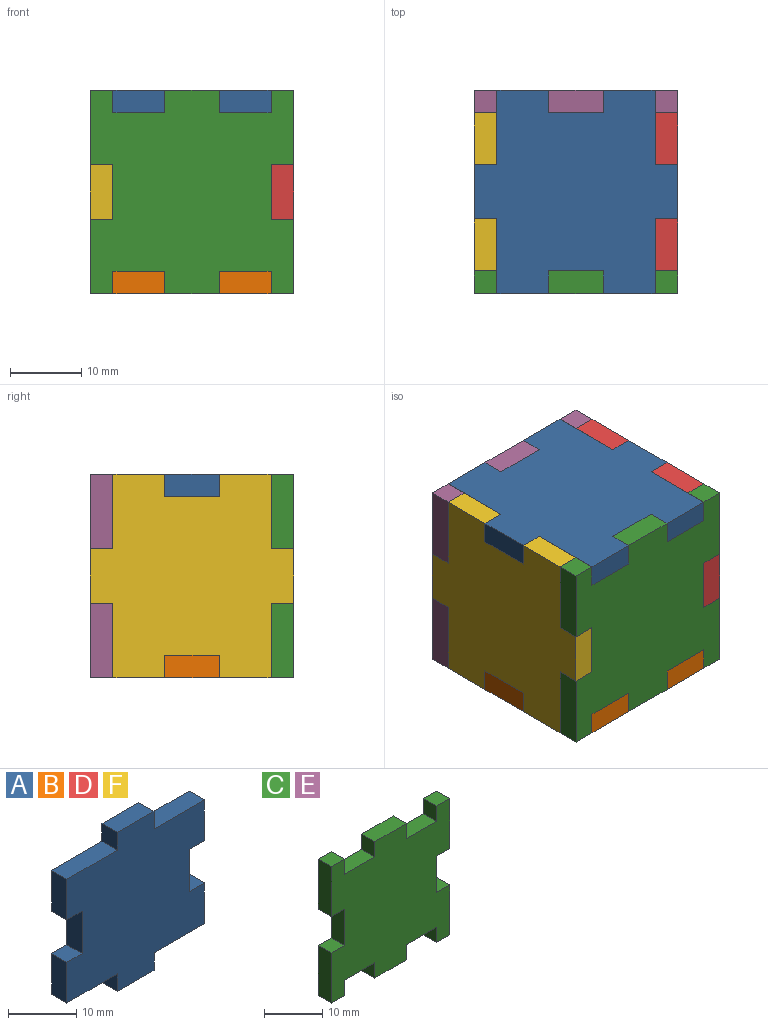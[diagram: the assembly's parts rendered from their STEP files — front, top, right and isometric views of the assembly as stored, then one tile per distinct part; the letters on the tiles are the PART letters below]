
ASSEMBLY  parts=6 mates=5
PART A: 22 faces, bbox 28.6x3.2x28.6 mm
  f0: plane 3.18x3.18mm, normal (-1,0,0), area 10.1mm2, adj f1,f19,f20,f21
  f1: plane 10.48x3.18mm, normal (0,0,1), area 33.3mm2, adj f0,f2,f20,f21
  f2: plane 7.3x3.18mm, normal (-1,0,0), area 23.2mm2, adj f1,f3,f20,f21
  f3: plane 3.18x3.18mm, normal (0,0,-1), area 10.1mm2, adj f2,f4,f20,f21
  f4: plane 7.62x3.18mm, normal (-1,0,0), area 24.2mm2, adj f3,f5,f20,f21
  f5: plane 3.18x3.18mm, normal (0,0,1), area 10.1mm2, adj f4,f6,f20,f21
  f6: plane 7.3x3.18mm, normal (-1,0,0), area 23.2mm2, adj f5,f7,f20,f21
  f7: plane 10.48x3.18mm, normal (0,0,-1), area 33.3mm2, adj f6,f8,f20,f21
  f8: plane 3.18x3.18mm, normal (-1,0,0), area 10.1mm2, adj f7,f9,f20,f21
  f9: plane 7.62x3.18mm, normal (0,0,-1), area 24.2mm2, adj f8,f10,f20,f21
  f10: plane 3.18x3.18mm, normal (1,0,0), area 10.1mm2, adj f9,f11,f20,f21
  f11: plane 10.48x3.18mm, normal (0,0,-1), area 33.3mm2, adj f10,f12,f20,f21
  f12: plane 7.3x3.18mm, normal (1,0,0), area 23.2mm2, adj f11,f13,f20,f21
  f13: plane 3.18x3.18mm, normal (0,0,1), area 10.1mm2, adj f12,f14,f20,f21
  f14: plane 7.62x3.18mm, normal (1,0,0), area 24.2mm2, adj f13,f15,f20,f21
  f15: plane 3.18x3.18mm, normal (0,0,-1), area 10.1mm2, adj f14,f16,f20,f21
  f16: plane 7.3x3.18mm, normal (1,0,0), area 23.2mm2, adj f15,f17,f20,f21
  f17: plane 10.48x3.18mm, normal (0,0,1), area 33.3mm2, adj f16,f18,f20,f21
  f18: plane 3.18x3.18mm, normal (1,0,0), area 10.1mm2, adj f17,f19,f20,f21
  f19: plane 7.62x3.18mm, normal (0,0,1), area 24.2mm2, adj f0,f18,f20,f21
  f20: plane 28.58x28.58mm, normal (0,-1,0), area 635.1mm2, adj f0,f1,f2,f3,f4,f5,f6,f7
  f21: plane 28.58x28.58mm, normal (0,1,0), area 635.1mm2, adj f0,f1,f2,f3,f4,f5,f6,f7
PART B: same geometry as A
PART C: 30 faces, bbox 28.6x3.2x28.6 mm
  f0: plane 3.18x3.18mm, normal (-1,0,0), area 10.1mm2, adj f1,f27,f28,f29
  f1: plane 7.3x3.18mm, normal (0,0,1), area 23.2mm2, adj f0,f2,f28,f29
  f2: plane 3.18x3.18mm, normal (1,0,0), area 10.1mm2, adj f1,f3,f28,f29
  f3: plane 3.18x3.18mm, normal (0,0,1), area 10.1mm2, adj f2,f4,f28,f29
  f4: plane 10.48x3.18mm, normal (-1,0,0), area 33.3mm2, adj f3,f5,f28,f29
  f5: plane 3.18x3.18mm, normal (0,0,-1), area 10.1mm2, adj f4,f6,f28,f29
  f6: plane 7.62x3.18mm, normal (-1,0,0), area 24.2mm2, adj f5,f7,f28,f29
  f7: plane 3.18x3.18mm, normal (0,0,1), area 10.1mm2, adj f6,f8,f28,f29
  f8: plane 10.48x3.18mm, normal (-1,0,0), area 33.3mm2, adj f7,f9,f28,f29
  f9: plane 3.18x3.18mm, normal (0,0,-1), area 10.1mm2, adj f8,f10,f28,f29
  f10: plane 3.18x3.18mm, normal (1,0,0), area 10.1mm2, adj f9,f11,f28,f29
  f11: plane 7.3x3.18mm, normal (0,0,-1), area 23.2mm2, adj f10,f12,f28,f29
  f12: plane 3.18x3.18mm, normal (-1,0,0), area 10.1mm2, adj f11,f13,f28,f29
  f13: plane 7.62x3.18mm, normal (0,0,-1), area 24.2mm2, adj f12,f14,f28,f29
  f14: plane 3.18x3.18mm, normal (1,0,0), area 10.1mm2, adj f13,f15,f28,f29
  f15: plane 7.3x3.18mm, normal (0,0,-1), area 23.2mm2, adj f14,f16,f28,f29
  f16: plane 3.18x3.18mm, normal (-1,0,0), area 10.1mm2, adj f15,f17,f28,f29
  f17: plane 3.18x3.18mm, normal (0,0,-1), area 10.1mm2, adj f16,f18,f28,f29
  f18: plane 10.48x3.18mm, normal (1,0,0), area 33.3mm2, adj f17,f19,f28,f29
  f19: plane 3.18x3.18mm, normal (0,0,1), area 10.1mm2, adj f18,f20,f28,f29
  f20: plane 7.62x3.18mm, normal (1,0,0), area 24.2mm2, adj f19,f21,f28,f29
  f21: plane 3.18x3.18mm, normal (0,0,-1), area 10.1mm2, adj f20,f22,f28,f29
  f22: plane 10.48x3.18mm, normal (1,0,0), area 33.3mm2, adj f21,f23,f28,f29
  f23: plane 3.18x3.18mm, normal (0,0,1), area 10.1mm2, adj f22,f24,f28,f29
  f24: plane 3.18x3.18mm, normal (-1,0,0), area 10.1mm2, adj f23,f25,f28,f29
  f25: plane 7.3x3.18mm, normal (0,0,1), area 23.2mm2, adj f24,f26,f28,f29
  f26: plane 3.18x3.18mm, normal (1,0,0), area 10.1mm2, adj f25,f27,f28,f29
  f27: plane 7.62x3.18mm, normal (0,0,1), area 24.2mm2, adj f0,f26,f28,f29
  f28: plane 28.58x28.58mm, normal (0,-1,0), area 675.4mm2, adj f0,f1,f2,f3,f4,f5,f6,f7
  f29: plane 28.58x28.58mm, normal (0,1,0), area 675.4mm2, adj f0,f1,f2,f3,f4,f5,f6,f7
PART D: same geometry as A
PART E: same geometry as C
PART F: same geometry as A
PLACE A rot(axis=(-0.58,0.58,-0.58),120deg) t=(-170.14,-28.31,78.36)mm
PLACE B rot(axis=(0.58,0.58,0.58),120deg) t=(-170.14,60.06,56.14)mm
PLACE C t=(-86.77,4.76,28.06)mm
PLACE D rot(axis=(-0.58,0.58,0.58),120deg) t=(-119.85,-23.31,23.06)mm
PLACE E t=(-86.77,30.16,28.06)mm
PLACE F rot(axis=(0.58,0.58,-0.58),120deg) t=(-142.07,55.06,23.06)mm
MATE fastened E.f28 <-> D.f1  axis (0,-1,0) through (-116.67,26.99,81.54)mm
MATE fastened D.f11 <-> C.f29  axis (0,-1,0) through (-116.67,4.76,52.96)mm
MATE fastened A.f17 <-> C.f24  axis (1,0,0) through (-119.85,1.59,81.54)mm
MATE fastened F.f21 <-> C.f6  axis (1,0,0) through (-142.07,1.59,71.06)mm
MATE fastened C.f15 <-> B.f21  axis (0,0,-1) through (-127.15,4.76,56.14)mm
